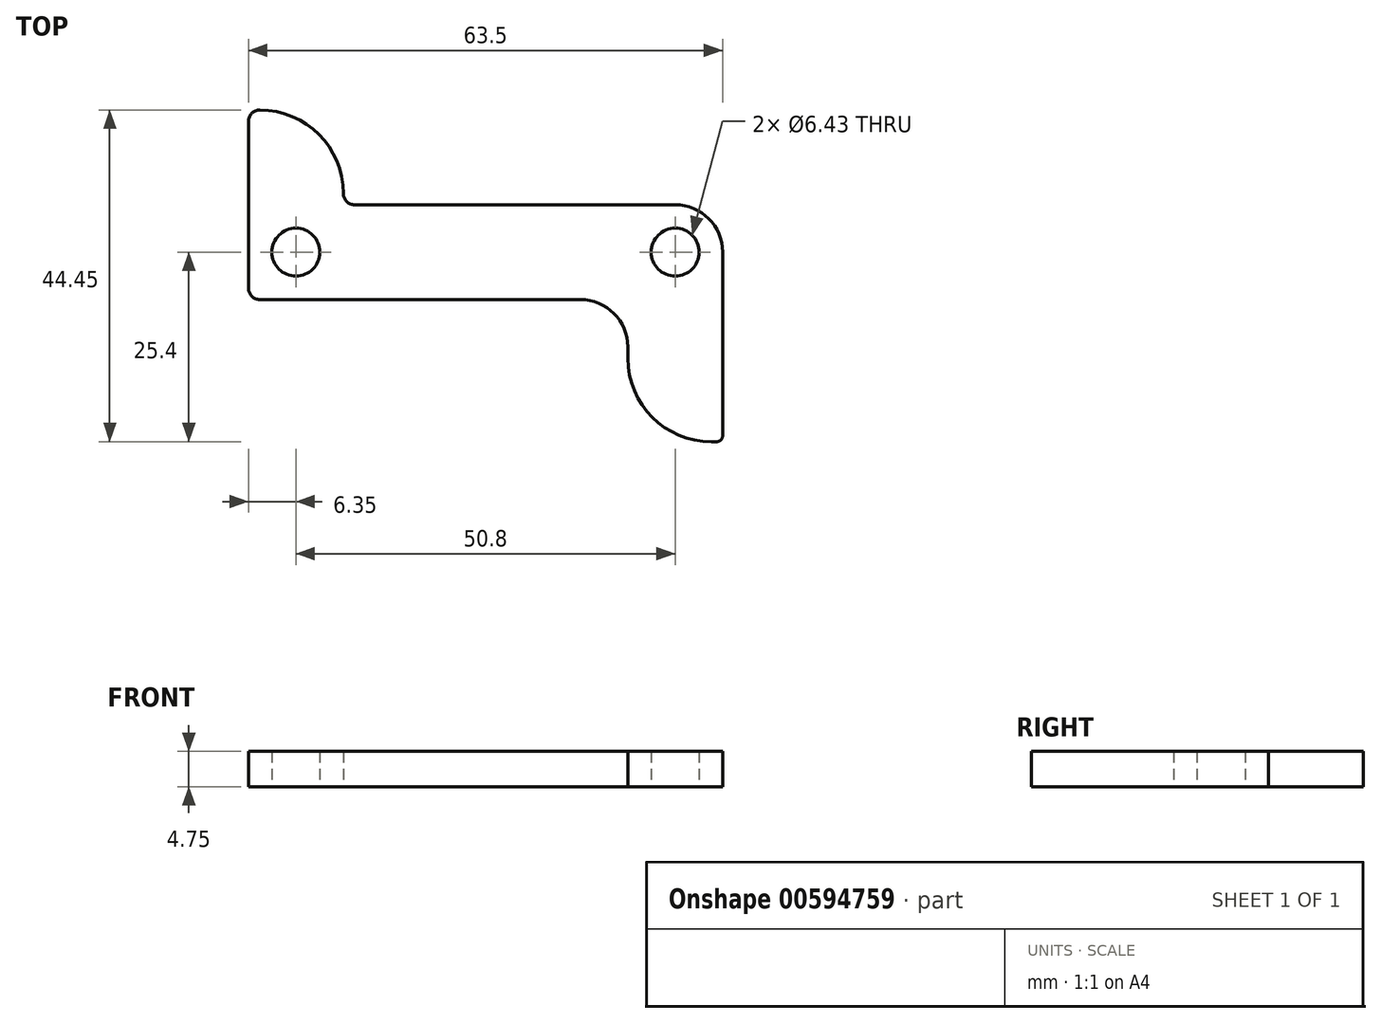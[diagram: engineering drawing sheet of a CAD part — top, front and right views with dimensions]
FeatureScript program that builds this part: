
annotation { "Feature Type Name" : "Feature", "Feature Type Description" : "" }
export const myFeature = defineFeature(function(context is Context, id is Id, definition is map)
    precondition{}
    {
        {
            var Q0;
            Q0=qCreatedBy(makeId("Top.planeOp"),FACE);
            var sketch = newSketch(context, id + "F0", { "sketchPlane" : qUnion([Q0])});
            skLineSegment(sketch, "E0", {"start": v(-31.75, 17.53) * mm, "end": v(-31.75, -4.83) * mm});
            skLineSegment(sketch, "E1", {"start": v(-30.23, -6.35) * mm, "end": v(12.7, -6.35) * mm});
            skLineSegment(sketch, "E2", {"start": v(19.05, -12.7) * mm, "end": v(19.05, -14.22) * mm});
            skLineSegment(sketch, "E3", {"start": v(30.23, -25.4) * mm, "end": v(30.99, -25.4) * mm});
            skLineSegment(sketch, "E4", {"start": v(31.75, -24.64) * mm, "end": v(31.75, 0) * mm});
            skLineSegment(sketch, "E5", {"start": v(25.4, 6.35) * mm, "end": v(-17.53, 6.35) * mm});
            skLineSegment(sketch, "E6", {"start": v(-19.05, 7.87) * mm, "end": v(-19.05, 7.87) * mm});
            skLineSegment(sketch, "E7", {"start": v(-30.23, 19.05) * mm, "end": v(-30.23, 19.05) * mm});
            skPoint(sketch, "E8.visualSharp", {"position": v(-19.05, 19.05) * mm});
            skArc(sketch, "E8.filletArc", {"start": v(-19.05, 7.87) * mm, "mid": v(-22.32, 15.78) * mm, "end": v(-30.23, 19.05) * mm});
            skPoint(sketch, "E9.visualSharp", {"position": v(19.05, -25.4) * mm});
            skArc(sketch, "E9.filletArc", {"start": v(19.05, -14.22) * mm, "mid": v(22.32, -22.13) * mm, "end": v(30.23, -25.4) * mm});
            skPoint(sketch, "E10.visualSharp", {"position": v(19.05, -6.35) * mm});
            skArc(sketch, "E10.filletArc", {"start": v(19.05, -12.7) * mm, "mid": v(17.2, -8.2) * mm, "end": v(12.7, -6.35) * mm});
            skPoint(sketch, "E11.visualSharp", {"position": v(31.75, 6.35) * mm});
            skArc(sketch, "E11.filletArc", {"start": v(31.75, 0) * mm, "mid": v(29.9, 4.5) * mm, "end": v(25.4, 6.35) * mm});
            skPoint(sketch, "E12.visualSharp", {"position": v(-31.75, 19.05) * mm});
            skArc(sketch, "E12.filletArc", {"start": v(-30.23, 19.05) * mm, "mid": v(-31.3, 18.6) * mm, "end": v(-31.75, 17.53) * mm});
            skPoint(sketch, "E13.visualSharp", {"position": v(-31.75, -6.35) * mm});
            skArc(sketch, "E13.filletArc", {"start": v(-31.75, -4.83) * mm, "mid": v(-31.3, -5.9) * mm, "end": v(-30.23, -6.35) * mm});
            skPoint(sketch, "E14.visualSharp", {"position": v(-19.05, 6.35) * mm});
            skArc(sketch, "E14.filletArc", {"start": v(-19.05, 7.87) * mm, "mid": v(-18.6, 6.8) * mm, "end": v(-17.53, 6.35) * mm});
            skPoint(sketch, "E15.visualSharp", {"position": v(31.75, -25.4) * mm});
            skArc(sketch, "E15.filletArc", {"start": v(30.99, -25.4) * mm, "mid": v(31.53, -25.18) * mm, "end": v(31.75, -24.64) * mm});
            skCircle(sketch, "E16", {"center": v(25.4, 0) * mm, "radius": 3.21 * mm});
            skCircle(sketch, "E17", {"center": v(-25.4, 0) * mm, "radius": 3.21 * mm});
            skSolve(sketch);
        }
        {
            var Q0;
            Q0 = qSketchRegion(id + "F0", true);
            extrude(context, id + "F1", {"entities" : qUnion([Q0]), "depth" : 4.75 * mm, "offsetDistance" : 25.4 * mm});
        }
    });
